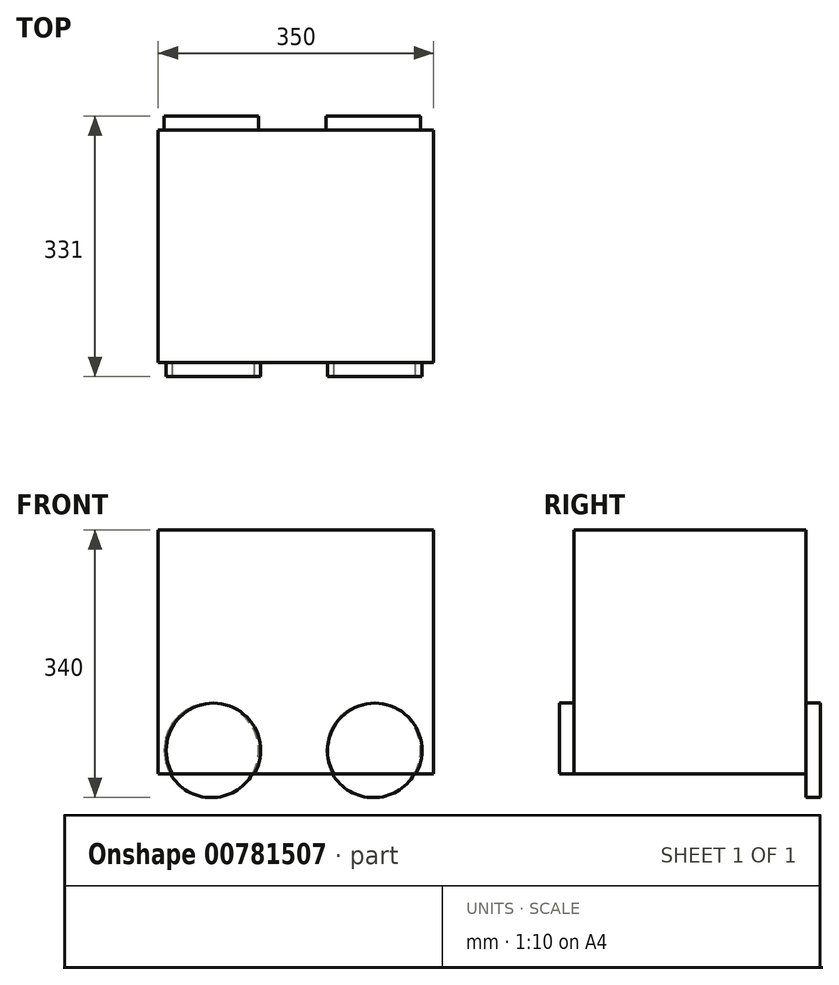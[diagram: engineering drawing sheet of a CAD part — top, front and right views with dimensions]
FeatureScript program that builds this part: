
annotation { "Feature Type Name" : "Feature", "Feature Type Description" : "" }
export const myFeature = defineFeature(function(context is Context, id is Id, definition is map)
    precondition{}
    {
        {
            var Q0;
            Q0=qCreatedBy(makeId("Front.planeOp"),FACE);
            var sketch = newSketch(context, id + "F0", { "sketchPlane" : qUnion([Q0])});
            skLineSegment(sketch, "E0.bottom", {"start": v(0, 0) * mm, "end": v(350, 0) * mm});
            skLineSegment(sketch, "E0.top", {"start": v(0, 310) * mm, "end": v(350, 310) * mm});
            skLineSegment(sketch, "E0.left", {"start": v(0, 0) * mm, "end": v(0, 310) * mm});
            skLineSegment(sketch, "E0.right", {"start": v(350, 0) * mm, "end": v(350, 310) * mm});
            skSolve(sketch);
        }
        {
            var Q0;
            Q0=makeQuery(id+"F0.imprint","IMPRINT",FACE,{"disambiguationData":[TD([[makeQuery(id+"F0.imprint","IMPRINT",EDGE,{"derivedFrom":sQuery(id+"F0.wireOp",EDGE,"E0.bottom")}),1.0]])]});
            extrude(context, id + "F1", {"entities" : qUnion([Q0]), "depth" : 295 * mm, "offsetDistance" : 25 * mm});
        }
        {
            var Q0;
            Q0=makeQuery(id+"F1.opExtrude","CAP_FACE",FACE,{"disambiguationData":[OSD([sQuery(id+"F0.wireOp",EDGE,"E0.bottom"),sQuery(id+"F0.wireOp",EDGE,"E0.top"),sQuery(id+"F0.wireOp",EDGE,"E0.left"),sQuery(id+"F0.wireOp",EDGE,"E0.right")])],"isStart":false});
            var sketch = newSketch(context, id + "F2", { "sketchPlane" : qUnion([Q0])});
            skLineSegment(sketch, "E1.0", {"start": v(0, 30) * mm, "end": v(350, 30) * mm});
            skCircle(sketch, "E2", {"center": v(70.2, 30) * mm, "radius": 60 * mm});
            skCircle(sketch, "E3", {"center": v(275.23, 30) * mm, "radius": 60 * mm});
            skSolve(sketch);
        }
        {
            var Q0;
            {var subQ0=sQuery(id+"F2.wireOp",EDGE,"E2");var subQ1=makeQuery(id+"F1.opExtrude","CAP_EDGE",EDGE,{"disambiguationData":[OSD([sQuery(id+"F0.wireOp",EDGE,"E0.bottom")])],"isStart":false});var subQ2=makeQuery(id+"F2.imprint","INTERSECT",VERTEX,{"disambiguationData":[OD(0.0)],"derivedFrom":[subQ1,subQ0]});Q0=makeQuery(id+"F2.imprint","IMPRINT",FACE,{"disambiguationData":[TD([[makeQuery(id+"F2.imprint","IMPRINT",EDGE,{"disambiguationData":[TD([[subQ2,-1.0]])],"derivedFrom":subQ0}),1.0]])]});}
            var Q1;
            {var subQ0=sQuery(id+"F2.wireOp",EDGE,"E3");var subQ1=makeQuery(id+"F1.opExtrude","CAP_EDGE",EDGE,{"disambiguationData":[OSD([sQuery(id+"F0.wireOp",EDGE,"E0.bottom")])],"isStart":false});var subQ2=makeQuery(id+"F2.imprint","INTERSECT",VERTEX,{"disambiguationData":[OD(0.0)],"derivedFrom":[subQ1,subQ0]});Q1=makeQuery(id+"F2.imprint","IMPRINT",FACE,{"disambiguationData":[TD([[makeQuery(id+"F2.imprint","IMPRINT",EDGE,{"disambiguationData":[TD([[subQ2,-1.0]])],"derivedFrom":subQ0}),1.0]])]});}
            var Q2;
            {var subQ0=sQuery(id+"F2.wireOp",EDGE,"E2");var subQ1=sQuery(id+"F2.wireOp",EDGE,"E1.0");var subQ2=makeQuery(id+"F2.imprint","INTERSECT",VERTEX,{"disambiguationData":[OD(0.0)],"derivedFrom":[subQ1,subQ0]});Q2=makeQuery(id+"F2.imprint","IMPRINT",FACE,{"disambiguationData":[TD([[makeQuery(id+"F2.imprint","IMPRINT",EDGE,{"disambiguationData":[TD([[subQ2,-1.0]])],"derivedFrom":subQ1}),-1.0]])]});}
            var Q3;
            {var subQ0=sQuery(id+"F2.wireOp",EDGE,"E3");var subQ1=sQuery(id+"F2.wireOp",EDGE,"E1.0");var subQ2=makeQuery(id+"F2.imprint","INTERSECT",VERTEX,{"disambiguationData":[OD(0.0)],"derivedFrom":[subQ1,subQ0]});Q3=makeQuery(id+"F2.imprint","IMPRINT",FACE,{"disambiguationData":[TD([[makeQuery(id+"F2.imprint","IMPRINT",EDGE,{"disambiguationData":[TD([[subQ2,-1.0]])],"derivedFrom":subQ1}),-1.0]])]});}
            var Q4;
            {var subQ0=sQuery(id+"F2.wireOp",EDGE,"E2");var subQ1=sQuery(id+"F2.wireOp",EDGE,"E1.0");var subQ2=makeQuery(id+"F2.imprint","INTERSECT",VERTEX,{"disambiguationData":[OD(0.0)],"derivedFrom":[subQ1,subQ0]});Q4=makeQuery(id+"F2.imprint","IMPRINT",FACE,{"disambiguationData":[TD([[makeQuery(id+"F2.imprint","IMPRINT",EDGE,{"disambiguationData":[TD([[subQ2,-1.0]])],"derivedFrom":subQ1}),1.0]])]});}
            var Q5;
            {var subQ0=sQuery(id+"F2.wireOp",EDGE,"E3");var subQ1=sQuery(id+"F2.wireOp",EDGE,"E1.0");var subQ2=makeQuery(id+"F2.imprint","INTERSECT",VERTEX,{"disambiguationData":[OD(0.0)],"derivedFrom":[subQ1,subQ0]});Q5=makeQuery(id+"F2.imprint","IMPRINT",FACE,{"disambiguationData":[TD([[makeQuery(id+"F2.imprint","IMPRINT",EDGE,{"disambiguationData":[TD([[subQ2,-1.0]])],"derivedFrom":subQ1}),1.0]])]});}
            extrude(context, id + "F3", {"entities" : qUnion([Q0, Q1, Q2, Q3, Q4, Q5]), "operationType" : NewBodyOperationType.ADD, "depth" : 18 * mm, "offsetDistance" : 25 * mm});
        }
        {
            var Q0;
            Q0=makeQuery(id+"F1.opExtrude","CAP_FACE",FACE,{"disambiguationData":[OSD([sQuery(id+"F0.wireOp",EDGE,"E0.bottom"),sQuery(id+"F0.wireOp",EDGE,"E0.top"),sQuery(id+"F0.wireOp",EDGE,"E0.left"),sQuery(id+"F0.wireOp",EDGE,"E0.right")])],"isStart":true});
            var sketch = newSketch(context, id + "F4", { "sketchPlane" : qUnion([Q0])});
            skLineSegment(sketch, "E4.0", {"start": v(0, 30) * mm, "end": v(-350, 30) * mm});
            skCircle(sketch, "E5", {"center": v(-273.5, 30) * mm, "radius": 60 * mm});
            skCircle(sketch, "E6", {"center": v(-67.61, 30) * mm, "radius": 60 * mm});
            skSolve(sketch);
        }
        {
            var Q0;
            Q0 = qSketchRegion(id + "F4", true);
            extrude(context, id + "F5", {"entities" : qUnion([Q0]), "operationType" : NewBodyOperationType.ADD, "depth" : 18 * mm, "offsetDistance" : 25 * mm});
        }
    });
